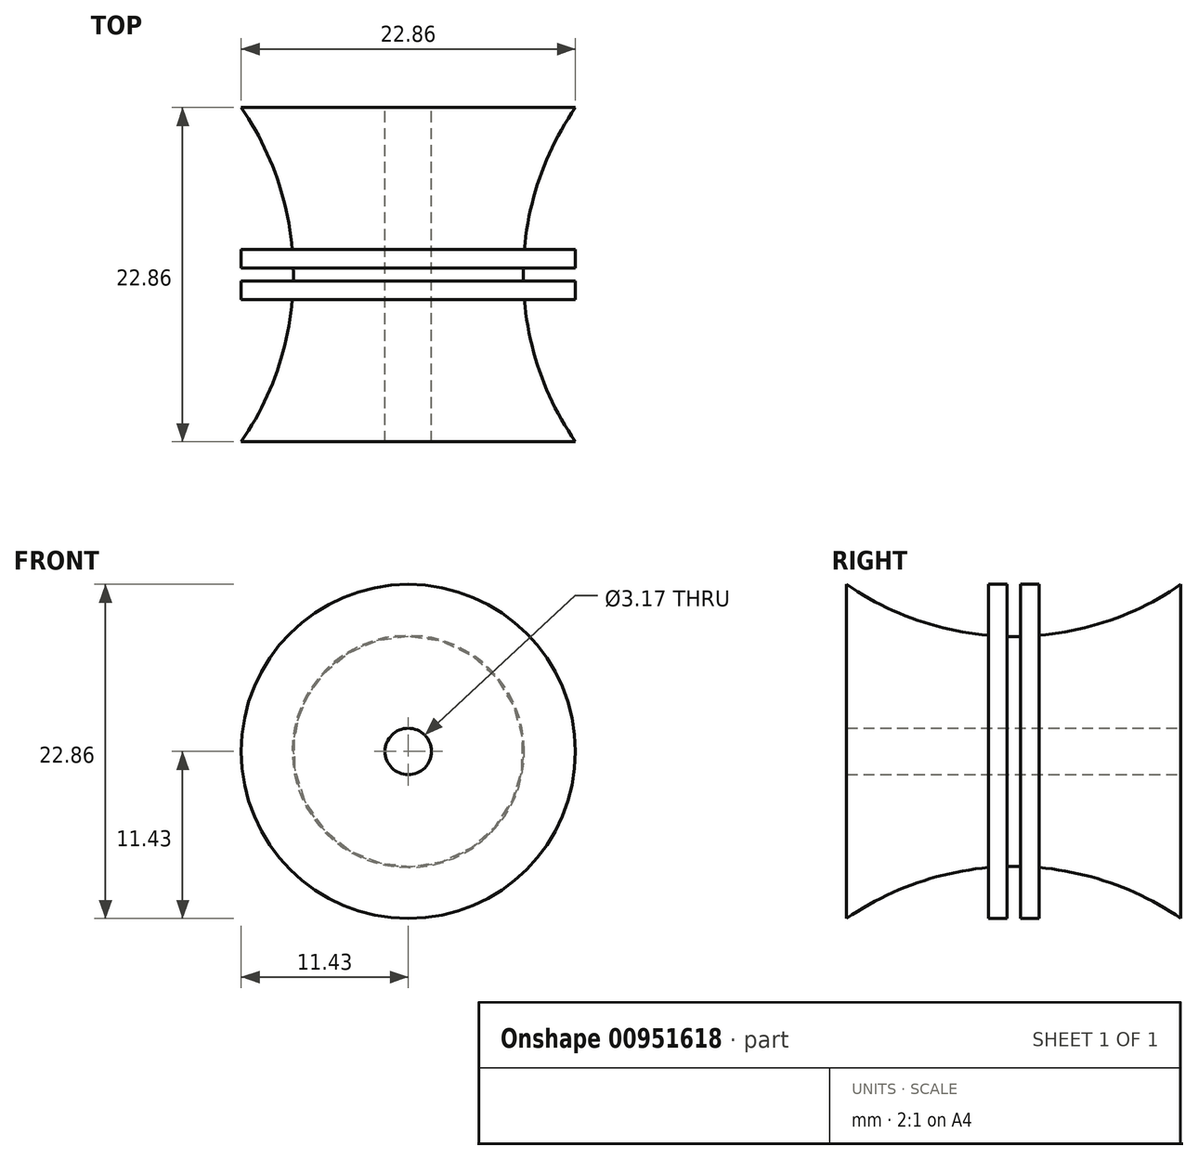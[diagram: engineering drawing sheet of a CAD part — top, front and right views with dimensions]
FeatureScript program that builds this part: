
annotation { "Feature Type Name" : "Feature", "Feature Type Description" : "" }
export const myFeature = defineFeature(function(context is Context, id is Id, definition is map)
    precondition{}
    {
        {
            assignVariable(context, id + "F0", {"name" : "Length", "anyValue" : 0.9});
        }
        {
            var Q0;
            Q0=qCreatedBy(makeId("Front.planeOp"),FACE);
            cPlane(context, id + "F1", {"entities" : qUnion([Q0]), "cplaneType" : CPlaneType.OFFSET, "offset" : (getVariable(context, 'Length') / 2) * mm, "width" : 150 * mm, "height" : 150 * mm});
        }
        {
            var Q0;
            Q0=qCreatedBy(id+"F1.planeOp",FACE);
            var sketch = newSketch(context, id + "F2", { "sketchPlane" : qUnion([Q0])});
            skCircle(sketch, "E0", {"center": v(0, 0) * mm, "radius": 11.43 * mm});
            skPoint(sketch, "E1", {"position": v(0, 11.43) * mm});
            skCircle(sketch, "E2", {"center": v(0, 0) * mm, "radius": 1.59 * mm});
            skPoint(sketch, "E3", {"position": v(0, 1.59) * mm});
            skSolve(sketch);
        }
        {
            var Q0;
            Q0=qSketchRegion(id+"F2",true);
            extrude(context, id + "F3", {"entities" : qUnion([Q0]), "depth" : 1.27 * mm, "offsetDistance" : 25.4 * mm});
        }
        {
            var Q0;
            Q0=qCreatedBy(makeId("Front.planeOp"),FACE);
            cPlane(context, id + "F4", {"entities" : qUnion([Q0]), "cplaneType" : CPlaneType.OFFSET, "offset" : (getVariable(context, 'Length') / 2) * mm, "oppositeDirection" : true, "width" : 152.4 * mm, "height" : 152.4 * mm});
        }
        {
            var Q0;
            Q0=qCreatedBy(id+"F4.planeOp",FACE);
            var sketch = newSketch(context, id + "F5", { "sketchPlane" : qUnion([Q0])});
            skCircle(sketch, "E4.0.0", {"center": v(0, 0) * mm, "radius": 11.43 * mm});
            skPoint(sketch, "E5", {"position": v(0, 11.43) * mm});
            skCircle(sketch, "E6.0", {"center": v(0, 0) * mm, "radius": 1.59 * mm});
            skPoint(sketch, "E7", {"position": v(0, 1.59) * mm});
            skSolve(sketch);
        }
        {
            var Q0;
            Q0=qSketchRegion(id+"F5",true);
            extrude(context, id + "F6", {"entities" : qUnion([Q0]), "operationType" : NewBodyOperationType.ADD, "oppositeDirection" : true, "depth" : 1.27 * mm, "offsetDistance" : 25.4 * mm});
        }
        {
            var Q0;
            Q0=qCreatedBy(makeId("Right.planeOp"),FACE);
            var sketch = newSketch(context, id + "F7", { "sketchPlane" : qUnion([Q0])});
            skArc(sketch, "E8", {"start": v(-11.43, 11.43) * mm, "mid": v(0, 7.86) * mm, "end": v(11.43, 11.43) * mm});
            skArc(sketch, "E9.MirrorCS", {"start": v(-11.43, -11.43) * mm, "mid": v(0, -7.86) * mm, "end": v(11.43, -11.43) * mm, "construction": true});
            skLineSegment(sketch, "E10.0", {"start": v(-11.43, -1.59) * mm, "end": v(-11.43, 1.59) * mm});
            skLineSegment(sketch, "E11.0", {"start": v(11.43, -1.59) * mm, "end": v(11.43, 1.59) * mm});
            skLineSegment(sketch, "E12", {"start": v(-11.43, 11.43) * mm, "end": v(-11.43, 1.59) * mm});
            skLineSegment(sketch, "E13", {"start": v(11.43, 11.43) * mm, "end": v(11.43, 1.59) * mm});
            skLineSegment(sketch, "E14", {"start": v(-11.43, 1.59) * mm, "end": v(11.43, 1.59) * mm});
            skLineSegment(sketch, "E15", {"start": v(11.43, 0) * mm, "end": v(-11.43, 0) * mm});
            skSolve(sketch);
        }
        {
            var Q0;
            Q0=makeQuery(id+"F7.imprint","IMPRINT",FACE,{"disambiguationData":[TD([[makeQuery(id+"F7.imprint","IMPRINT",EDGE,{"derivedFrom":sQuery(id+"F7.wireOp",EDGE,"E8")}),-1.0]])]});
            var Q1;
            Q1=sQuery(id+"F7.wireOp",EDGE,"E15");
            revolve(context, id + "F8", {"operationType" : NewBodyOperationType.ADD, "surfaceOperationType" : NewSurfaceOperationType.NEW, "entities" : qUnion([Q0]), "axis" : qUnion([Q1]), "revolveType" : RevolveType.FULL});
        }
    });
